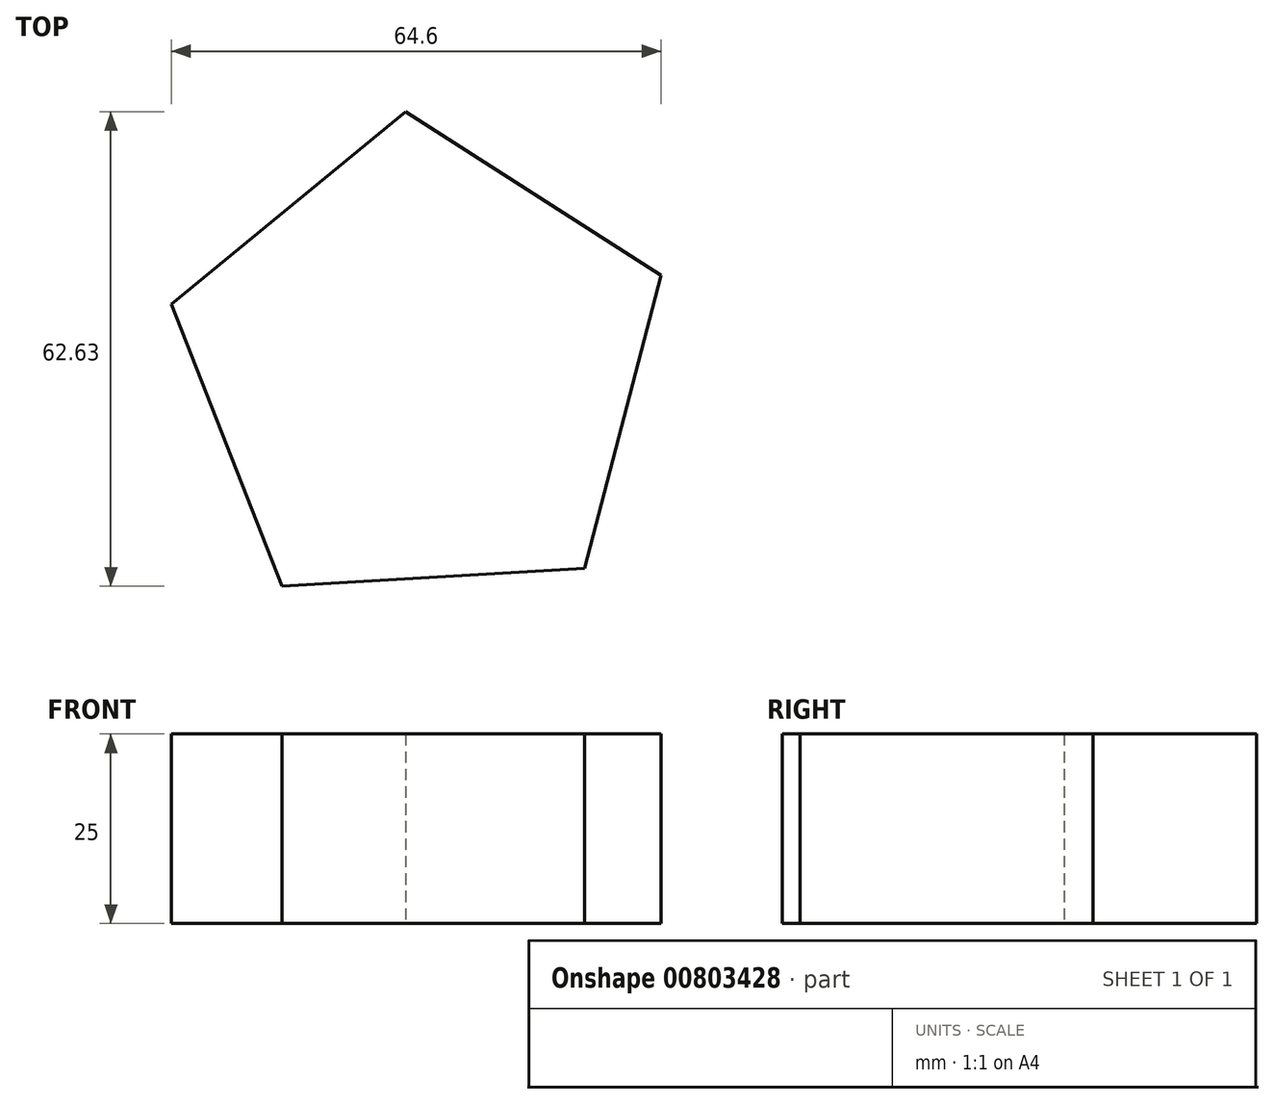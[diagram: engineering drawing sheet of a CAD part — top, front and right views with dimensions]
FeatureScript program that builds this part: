
annotation { "Feature Type Name" : "Feature", "Feature Type Description" : "" }
export const myFeature = defineFeature(function(context is Context, id is Id, definition is map)
    precondition{}
    {
        {
            var Q0;
            Q0=qCreatedBy(makeId("Top.planeOp"),FACE);
            var sketch = newSketch(context, id + "F0", { "sketchPlane" : qUnion([Q0])});
            skCircle(sketch, "E0.cCircle", {"center": v(0, 0) * mm, "radius": 27.53 * mm, "construction": true});
            skLineSegment(sketch, "E0.0", {"start": v(21.58, -26.3) * mm, "end": v(-18.35, -28.66) * mm});
            skLineSegment(sketch, "E0.1", {"start": v(-18.35, -28.66) * mm, "end": v(-32.92, 8.6) * mm});
            skLineSegment(sketch, "E0.2", {"start": v(-32.92, 8.6) * mm, "end": v(-2, 33.97) * mm});
            skLineSegment(sketch, "E0.3", {"start": v(-2, 33.97) * mm, "end": v(31.68, 12.4) * mm});
            skLineSegment(sketch, "E0.4", {"start": v(31.68, 12.4) * mm, "end": v(21.58, -26.3) * mm});
            skPoint(sketch, "E0.0.midPoint", {"position": v(1.62, -27.48) * mm});
            skSolve(sketch);
        }
        {
            var Q0;
            Q0=makeQuery(id+"F0.imprint","IMPRINT",FACE,{"disambiguationData":[TD([[makeQuery(id+"F0.imprint","IMPRINT",EDGE,{"derivedFrom":sQuery(id+"F0.wireOp",EDGE,"E0.0")}),-1.0]])]});
            extrude(context, id + "F1", {"entities" : qUnion([Q0]), "depth" : 25 * mm, "offsetDistance" : 25 * mm});
        }
    });
